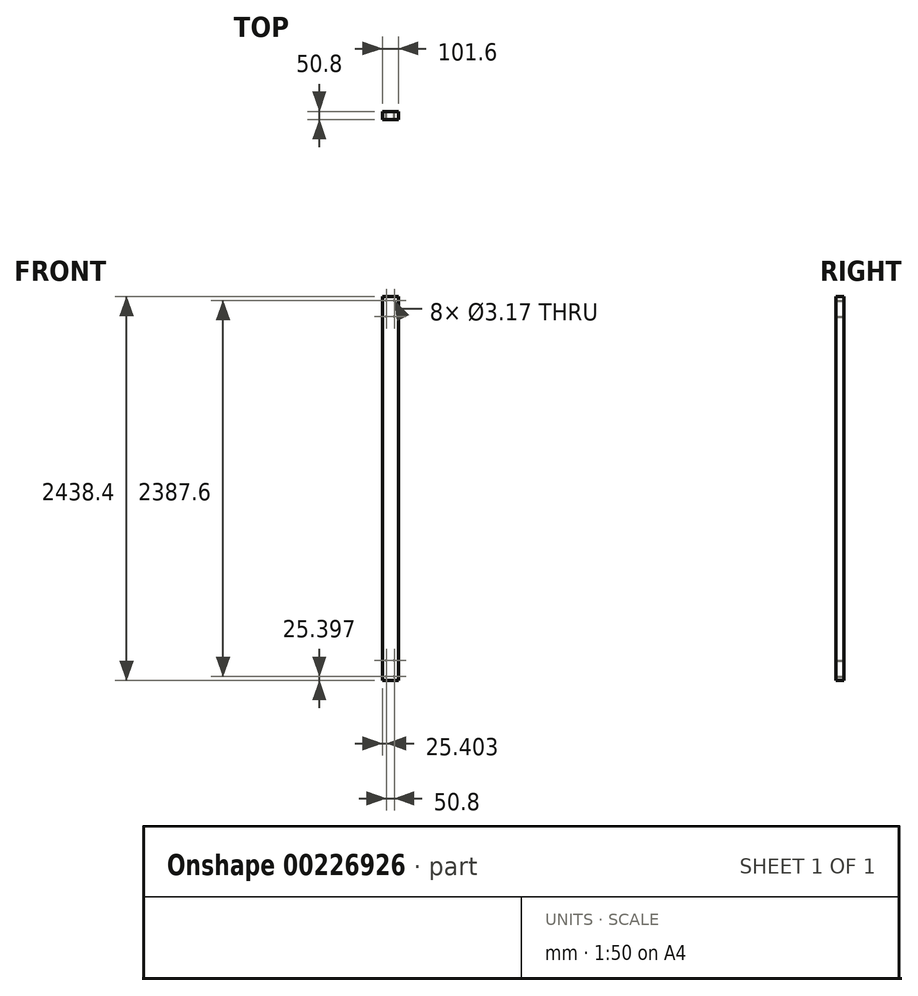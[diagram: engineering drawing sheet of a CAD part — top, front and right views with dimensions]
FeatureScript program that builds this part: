
annotation { "Feature Type Name" : "Feature", "Feature Type Description" : "" }
export const myFeature = defineFeature(function(context is Context, id is Id, definition is map)
    precondition{}
    {
        {
            var Q0;
            Q0=qCreatedBy(makeId("Front.planeOp"),FACE);
            var sketch = newSketch(context, id + "F0", { "sketchPlane" : qUnion([Q0])});
            skLineSegment(sketch, "E0.bottom", {"start": v(-51.57, 2308.87) * mm, "end": v(50.03, 2308.87) * mm});
            skLineSegment(sketch, "E0.top", {"start": v(-51.57, -129.53) * mm, "end": v(50.03, -129.53) * mm});
            skLineSegment(sketch, "E0.left", {"start": v(-51.57, 2308.87) * mm, "end": v(-51.57, -129.53) * mm});
            skLineSegment(sketch, "E0.right", {"start": v(50.03, 2308.87) * mm, "end": v(50.03, -129.53) * mm});
            skCircle(sketch, "E1", {"center": v(-26.17, 2283.47) * mm, "radius": 1.59 * mm});
            skCircle(sketch, "E2", {"center": v(24.63, 2283.47) * mm, "radius": 1.59 * mm});
            skCircle(sketch, "E3", {"center": v(-26.17, 2181.87) * mm, "radius": 1.59 * mm});
            skCircle(sketch, "E4", {"center": v(24.63, 2181.87) * mm, "radius": 1.59 * mm});
            skCircle(sketch, "E5", {"center": v(24.63, -104.13) * mm, "radius": 1.59 * mm});
            skCircle(sketch, "E6", {"center": v(-26.17, -104.13) * mm, "radius": 1.59 * mm});
            skCircle(sketch, "E7", {"center": v(24.63, -2.53) * mm, "radius": 1.59 * mm});
            skCircle(sketch, "E8", {"center": v(-26.17, -2.53) * mm, "radius": 1.59 * mm});
            skSolve(sketch);
        }
        {
            var Q0;
            Q0 = qSketchRegion(id + "F0", true);
            extrude(context, id + "F1", {"entities" : qUnion([Q0]), "depth" : 50.8 * mm});
        }
    });
